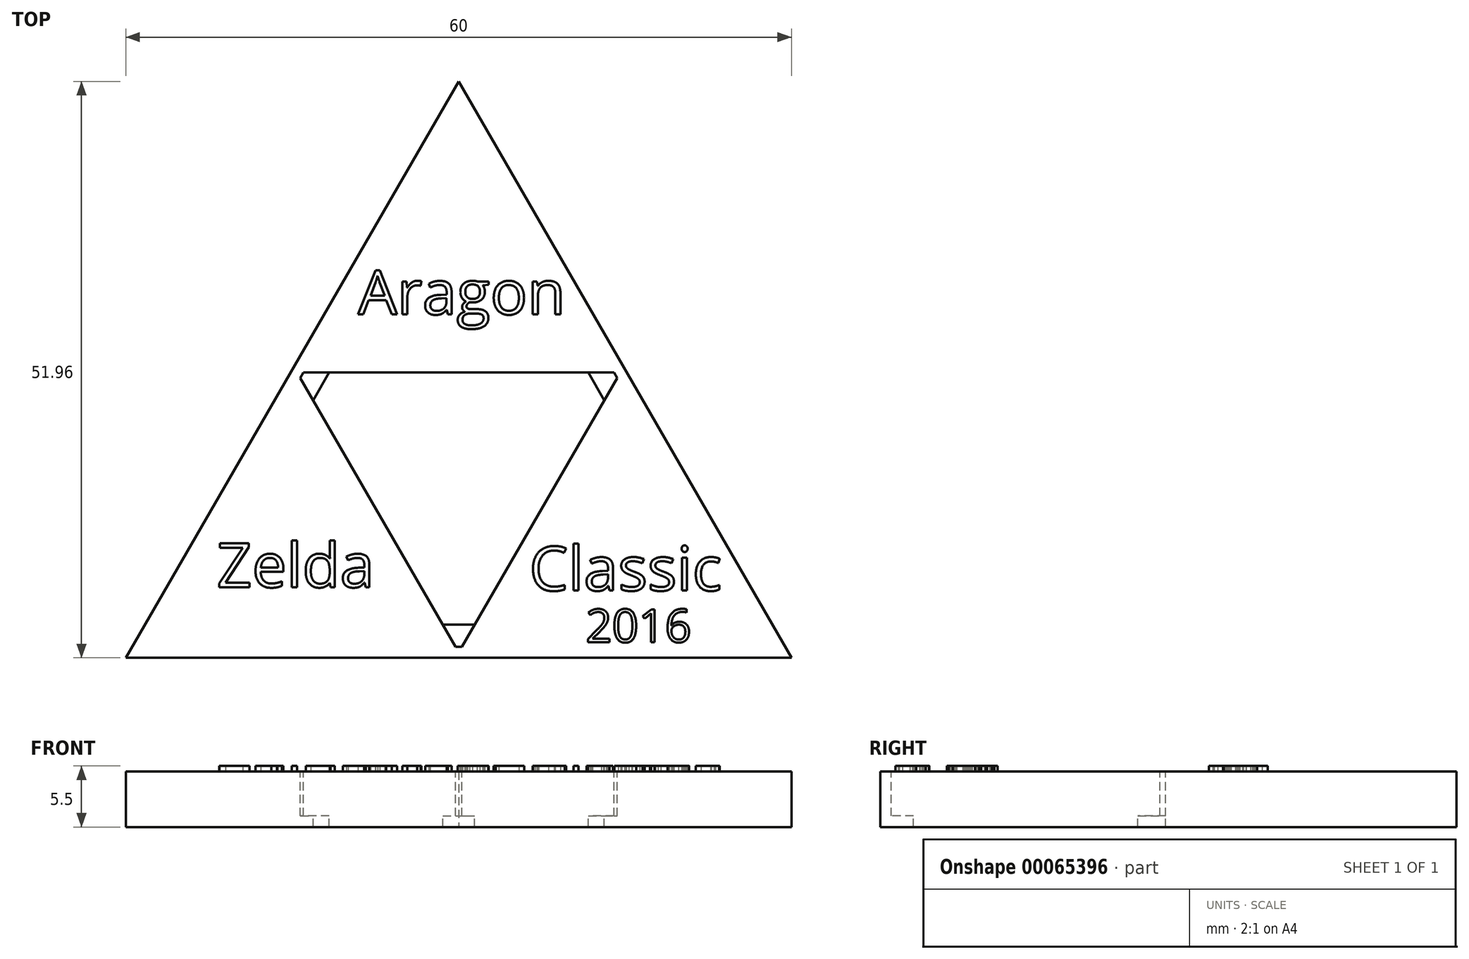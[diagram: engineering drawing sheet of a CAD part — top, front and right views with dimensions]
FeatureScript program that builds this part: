
annotation { "Feature Type Name" : "Feature", "Feature Type Description" : "" }
export const myFeature = defineFeature(function(context is Context, id is Id, definition is map)
    precondition{}
    {
        {
            var Q0;
            Q0=qCreatedBy(makeId("Top.planeOp"),FACE);
            var sketch = newSketch(context, id + "F0", { "sketchPlane" : qUnion([Q0])});
            skLineSegment(sketch, "E0", {"start": v(-30, -21.96) * mm, "end": v(30, -21.96) * mm});
            skLineSegment(sketch, "E1", {"start": v(30, -21.96) * mm, "end": v(0, 30) * mm});
            skLineSegment(sketch, "E2", {"start": v(0, 30) * mm, "end": v(-30, -21.96) * mm});
            skSolve(sketch);
        }
        {
            var Q0;
            Q0=makeQuery(id+"F0.imprint","IMPRINT",FACE,{"disambiguationData":[TD([[makeQuery(id+"F0.imprint","IMPRINT",EDGE,{"derivedFrom":sQuery(id+"F0.wireOp",EDGE,"E0")}),1.0]])]});
            extrude(context, id + "F1", {"entities" : qUnion([Q0]), "depth" : 5 * mm});
        }
        {
            var Q0;
            Q0=makeQuery(id+"F1.opExtrude","CAP_FACE",FACE,{"disambiguationData":[OSD([sQuery(id+"F0.wireOp",EDGE,"E0"),sQuery(id+"F0.wireOp",EDGE,"E1"),sQuery(id+"F0.wireOp",EDGE,"E2")])],"isStart":false});
            var sketch = newSketch(context, id + "F2", { "sketchPlane" : qUnion([Q0])});
            skLineSegment(sketch, "E3", {"start": v(-14.28, 3.27) * mm, "end": v(-0.29, -20.96) * mm});
            skLineSegment(sketch, "E4", {"start": v(0.29, -20.96) * mm, "end": v(14.28, 3.27) * mm});
            skLineSegment(sketch, "E5", {"start": v(13.99, 3.77) * mm, "end": v(-13.99, 3.77) * mm});
            skLineSegment(sketch, "E6", {"start": v(-13.99, 3.77) * mm, "end": v(-14.28, 3.27) * mm});
            skLineSegment(sketch, "E7", {"start": v(13.99, 3.77) * mm, "end": v(14.28, 3.27) * mm});
            skLineSegment(sketch, "E8", {"start": v(-0.29, -20.96) * mm, "end": v(0.29, -20.96) * mm});
            skSolve(sketch);
        }
        {
            var Q0;
            Q0=makeQuery(id+"F2.imprint","IMPRINT",FACE,{"disambiguationData":[TD([[makeQuery(id+"F2.imprint","IMPRINT",EDGE,{"derivedFrom":sQuery(id+"F2.wireOp",EDGE,"E3")}),1.0]])]});
            extrude(context, id + "F3", {"entities" : qUnion([Q0]), "operationType" : NewBodyOperationType.REMOVE, "oppositeDirection" : true, "depth" : 4 * mm});
        }
        {
            var Q0;
            Q0=makeQuery(id+"F3.boolean.opBoolean","COPY",FACE,{"derivedFrom":makeQuery(id+"F3.opExtrude","CAP_FACE",FACE,{"disambiguationData":[OSD([sQuery(id+"F2.wireOp",EDGE,"E3"),sQuery(id+"F2.wireOp",EDGE,"E4"),sQuery(id+"F2.wireOp",EDGE,"E5"),sQuery(id+"F2.wireOp",EDGE,"E6"),sQuery(id+"F2.wireOp",EDGE,"E7"),sQuery(id+"F2.wireOp",EDGE,"E8")])],"isStart":false})});
            var sketch = newSketch(context, id + "F4", { "sketchPlane" : qUnion([Q0])});
            skLineSegment(sketch, "E9", {"start": v(11.68, 3.77) * mm, "end": v(13.12, 1.27) * mm});
            skLineSegment(sketch, "E10", {"start": v(-11.68, 3.77) * mm, "end": v(-13.12, 1.27) * mm});
            skLineSegment(sketch, "E11", {"start": v(-1.44, -18.96) * mm, "end": v(1.44, -18.96) * mm});
            skSolve(sketch);
        }
        {
            var Q0;
            {var subQ3=sQuery(id+"F4.wireOp",EDGE,"E9");Q0=makeQuery(id+"F4.imprint","IMPRINT",FACE,{"disambiguationData":[TD([[makeQuery(id+"F4.imprint","IMPRINT",EDGE,{"derivedFrom":subQ3}),-1.0]])]});}
            extrude(context, id + "F5", {"entities" : qUnion([Q0]), "operationType" : NewBodyOperationType.REMOVE, "oppositeDirection" : true, "depth" : 25 * mm});
        }
        {
            var Q0;
            Q0=makeQuery(id+"F1.opExtrude","CAP_FACE",FACE,{"disambiguationData":[OSD([sQuery(id+"F0.wireOp",EDGE,"E0"),sQuery(id+"F0.wireOp",EDGE,"E1"),sQuery(id+"F0.wireOp",EDGE,"E2")])],"isStart":false});
            var sketch = newSketch(context, id + "F6", { "sketchPlane" : qUnion([Q0])});
            skText(sketch, "E12", { "text": "Aragon", "fontName": "OpenSans-Regular.ttf"});
            skText(sketch, "E13", { "text": "Zelda", "fontName": "OpenSans-Regular.ttf"});
            skText(sketch, "E14", { "text": "Classic", "fontName": "OpenSans-Regular.ttf"});
            skText(sketch, "E15", { "text": "2016", "fontName": "OpenSans-Regular.ttf"});
            const initialGuessF6  = {"E12": [-0.00907, 0.009, 1, 0, 0.004], "E13": [-0.0218, -0.0156, 1, 0, 0.004], "E14": [0.00636, -0.0159, 1, 0, 0.004], "E15": [0.01144, -0.02056, 1, 0, 0.003]};
            skSetInitialGuess(sketch, initialGuessF6);
            skSolve(sketch);
        }
        {
            var Q0;
            Q0 = qSketchRegion(id + "F6", true);
            extrude(context, id + "F7", {"entities" : qUnion([Q0]), "operationType" : NewBodyOperationType.ADD, "depth" : .5 * mm});
        }
    });
